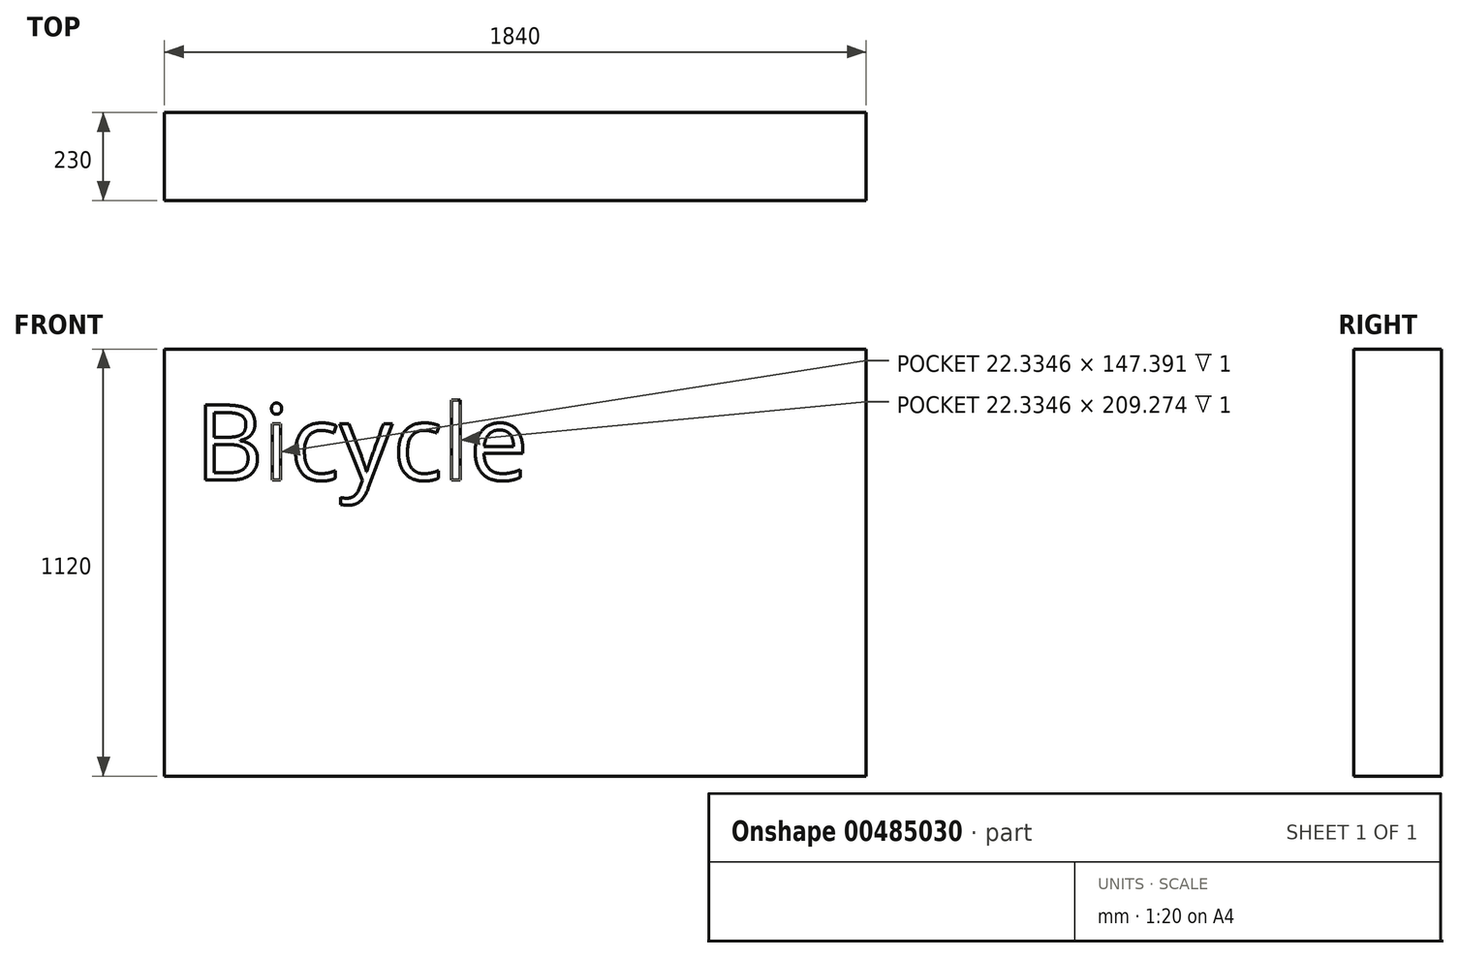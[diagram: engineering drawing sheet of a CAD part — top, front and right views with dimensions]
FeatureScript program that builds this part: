
annotation { "Feature Type Name" : "Feature", "Feature Type Description" : "" }
export const myFeature = defineFeature(function(context is Context, id is Id, definition is map)
    precondition{}
    {
        {
            var Q0;
            Q0=qCreatedBy(makeId("Front.planeOp"),FACE);
            var sketch = newSketch(context, id + "F0", { "sketchPlane" : qUnion([Q0])});
            skLineSegment(sketch, "E0.bottom", {"start": v(0, 0) * mm, "end": v(1840, 0) * mm});
            skLineSegment(sketch, "E0.top", {"start": v(0, 1120) * mm, "end": v(1840, 1120) * mm});
            skLineSegment(sketch, "E0.left", {"start": v(0, 0) * mm, "end": v(0, 1120) * mm});
            skLineSegment(sketch, "E0.right", {"start": v(1840, 0) * mm, "end": v(1840, 1120) * mm});
            skSolve(sketch);
        }
        {
            var Q0;
            Q0=makeQuery(id+"F0.imprint","IMPRINT",FACE,{"disambiguationData":[TD([[makeQuery(id+"F0.imprint","IMPRINT",EDGE,{"derivedFrom":sQuery(id+"F0.wireOp",EDGE,"E0.bottom")}),1.0]])]});
            extrude(context, id + "F1", {"entities" : qUnion([Q0]), "depth" : 230 * mm, "offsetDistance" : 25 * mm});
        }
        {
            var Q0;
            Q0=makeQuery(id+"F1.opExtrude","CAP_FACE",FACE,{"disambiguationData":[OSD([sQuery(id+"F0.wireOp",EDGE,"E0.bottom"),sQuery(id+"F0.wireOp",EDGE,"E0.top"),sQuery(id+"F0.wireOp",EDGE,"E0.left"),sQuery(id+"F0.wireOp",EDGE,"E0.right")])],"isStart":false});
            var sketch = newSketch(context, id + "F2", { "sketchPlane" : qUnion([Q0])});
            skText(sketch, "E1", { "text": "Bicycle\n", "fontName": "OpenSans-Regular.ttf"});
            const initialGuessF2  = {"E1": [0.08037, 0.77641, 1, 0, 0.1983]};
            skSetInitialGuess(sketch, initialGuessF2);
            skSolve(sketch);
        }
        {
            var Q0;
            Q0 = qSketchRegion(id + "F2", true);
            extrude(context, id + "F3", {"entities" : qUnion([Q0]), "operationType" : NewBodyOperationType.REMOVE, "oppositeDirection" : true, "depth" : 1 * mm, "offsetDistance" : 25 * mm});
        }
    });
